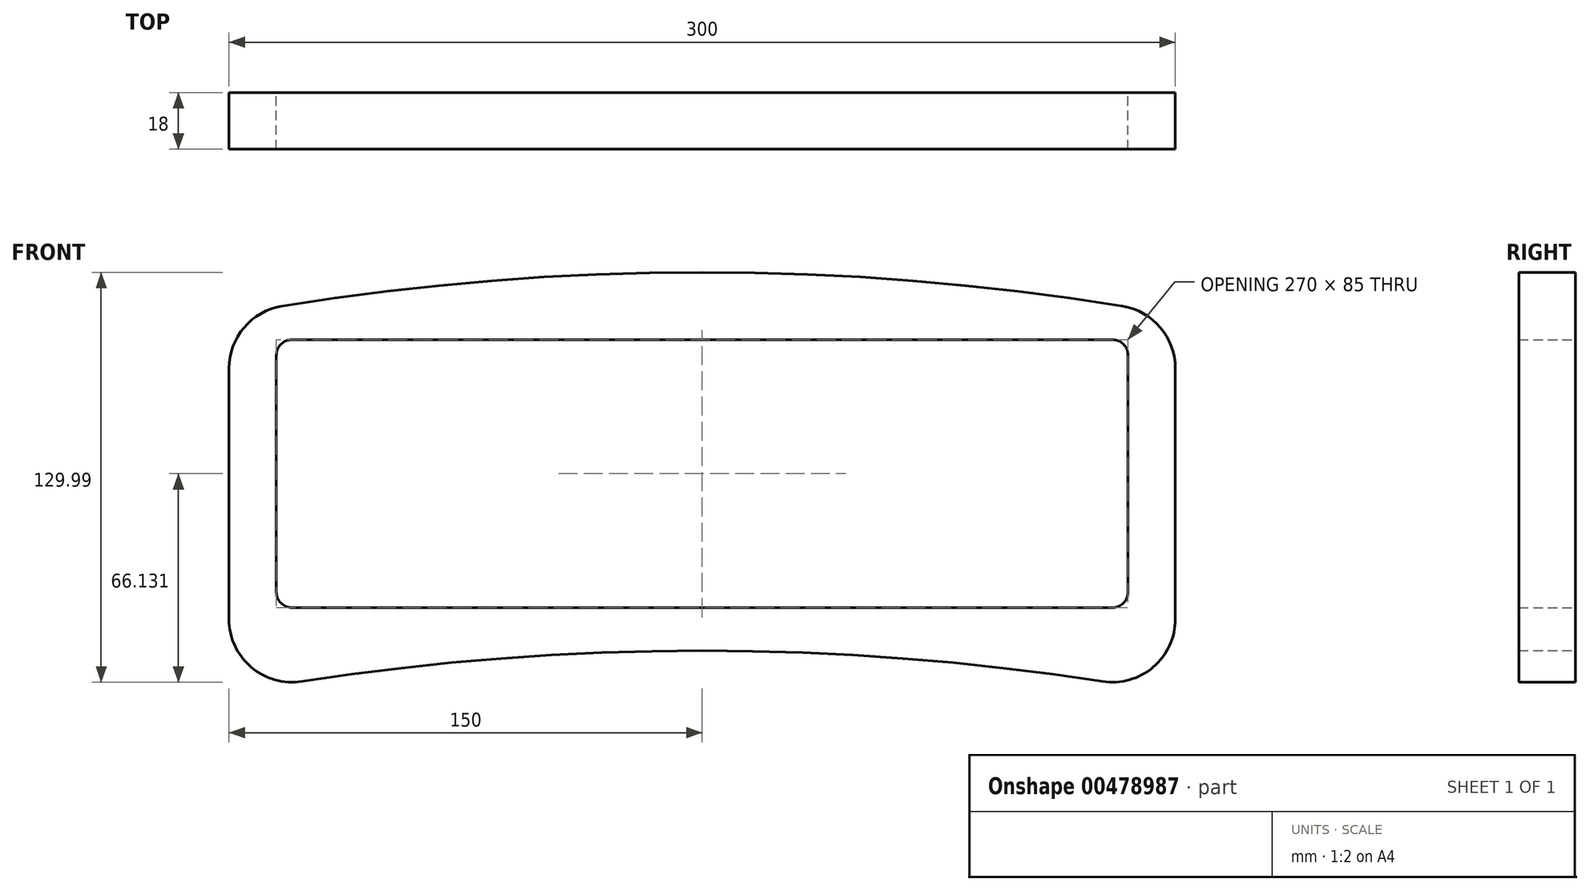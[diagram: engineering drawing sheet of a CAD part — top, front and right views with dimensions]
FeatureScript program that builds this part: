
annotation { "Feature Type Name" : "Feature", "Feature Type Description" : "" }
export const myFeature = defineFeature(function(context is Context, id is Id, definition is map)
    precondition{}
    {
        {
            var Q0;
            Q0=qCreatedBy(makeId("Front.planeOp"),FACE);
            var sketch = newSketch(context, id + "F0", { "sketchPlane" : qUnion([Q0])});
            skLineSegment(sketch, "E0", {"start": v(-80, 2.1) * mm, "end": v(80, 2.1) * mm, "construction": true});
            skLineSegment(sketch, "E1.bottom", {"start": v(-119, -36.9) * mm, "end": v(-41, -36.9) * mm, "construction": true});
            skLineSegment(sketch, "E1.top", {"start": v(-119, 41.1) * mm, "end": v(-41, 41.1) * mm, "construction": true});
            skLineSegment(sketch, "E1.left", {"start": v(-119, -36.9) * mm, "end": v(-119, 41.1) * mm, "construction": true});
            skLineSegment(sketch, "E1.right", {"start": v(-41, -36.9) * mm, "end": v(-41, 41.1) * mm, "construction": true});
            skPoint(sketch, "E1.middle", {"position": v(-80, 2.1) * mm});
            skLineSegment(sketch, "E2.bottom", {"start": v(119, -36.9) * mm, "end": v(41, -36.9) * mm, "construction": true});
            skLineSegment(sketch, "E2.top", {"start": v(119, 41.1) * mm, "end": v(41, 41.1) * mm, "construction": true});
            skLineSegment(sketch, "E2.left", {"start": v(119, -36.9) * mm, "end": v(119, 41.1) * mm, "construction": true});
            skLineSegment(sketch, "E2.right", {"start": v(41, -36.9) * mm, "end": v(41, 41.1) * mm, "construction": true});
            skPoint(sketch, "E2.middle", {"position": v(80, 2.1) * mm});
            skCircle(sketch, "E3", {"center": v(-80, 2.1) * mm, "radius": 37 * mm, "construction": true});
            skCircle(sketch, "E4", {"center": v(80, 2.1) * mm, "radius": 37 * mm, "construction": true});
            skLineSegment(sketch, "E5", {"start": v(-150, 35.47) * mm, "end": v(-150, -44.04) * mm});
            skLineSegment(sketch, "E6", {"start": v(0, 65.95) * mm, "end": v(0, -54.05) * mm, "construction": true});
            skLineSegment(sketch, "E7", {"start": v(150, 35.47) * mm, "end": v(150, -44.04) * mm});
            skPoint(sketch, "E8", {"position": v(-150, -7.7) * mm});
            skPoint(sketch, "E9", {"position": v(150, -7.7) * mm});
            skPoint(sketch, "E10", {"position": v(0, 5.95) * mm});
            skArc(sketch, "E11", {"start": v(133.2, 55.2) * mm, "mid": v(0, 65.95) * mm, "end": v(-133.2, 55.2) * mm});
            skArc(sketch, "E12", {"start": v(150, -7.7) * mm, "mid": v(0, 5.95) * mm, "end": v(-150, -7.7) * mm, "construction": true});
            skArc(sketch, "E13", {"start": v(126.95, -63.8) * mm, "mid": v(0, -54.05) * mm, "end": v(-126.95, -63.8) * mm});
            skPoint(sketch, "E14.visualSharp", {"position": v(-150, 52.3) * mm});
            skArc(sketch, "E14.filletArc", {"start": v(-133.2, 55.2) * mm, "mid": v(-145.23, 48.43) * mm, "end": v(-150, 35.47) * mm});
            skPoint(sketch, "E15.visualSharp", {"position": v(150, 52.3) * mm});
            skArc(sketch, "E15.filletArc", {"start": v(150, 35.47) * mm, "mid": v(145.23, 48.43) * mm, "end": v(133.2, 55.2) * mm});
            skPoint(sketch, "E16.visualSharp", {"position": v(150, -67.7) * mm});
            skArc(sketch, "E16.filletArc", {"start": v(126.95, -63.8) * mm, "mid": v(143.02, -59.22) * mm, "end": v(150, -44.04) * mm});
            skPoint(sketch, "E17.visualSharp", {"position": v(-150, -67.7) * mm});
            skArc(sketch, "E17.filletArc", {"start": v(-150, -44.04) * mm, "mid": v(-143.02, -59.22) * mm, "end": v(-126.95, -63.8) * mm});
            skLineSegment(sketch, "E18", {"start": v(-119, 41.1) * mm, "end": v(-41, -36.9) * mm, "construction": true});
            skLineSegment(sketch, "E19", {"start": v(-41, 41.1) * mm, "end": v(-119, -36.9) * mm, "construction": true});
            skLineSegment(sketch, "E20", {"start": v(41, 41.1) * mm, "end": v(119, -36.9) * mm, "construction": true});
            skLineSegment(sketch, "E21", {"start": v(119, 41.1) * mm, "end": v(41, -36.9) * mm, "construction": true});
            skCircle(sketch, "E22", {"center": v(-80, 2.1) * mm, "radius": 42.5 * mm, "construction": true});
            skCircle(sketch, "E23", {"center": v(80, 2.1) * mm, "radius": 42.5 * mm, "construction": true});
            skCircle(sketch, "E24", {"center": v(-49.95, 32.14) * mm, "radius": 2 * mm, "construction": true});
            skCircle(sketch, "E25", {"center": v(-110.05, 32.14) * mm, "radius": 2 * mm, "construction": true});
            skCircle(sketch, "E26", {"center": v(-110.05, -27.96) * mm, "radius": 2 * mm, "construction": true});
            skCircle(sketch, "E27", {"center": v(-49.95, -27.96) * mm, "radius": 2 * mm, "construction": true});
            skCircle(sketch, "E28", {"center": v(49.95, 32.14) * mm, "radius": 2 * mm, "construction": true});
            skCircle(sketch, "E29", {"center": v(49.95, -27.96) * mm, "radius": 2 * mm, "construction": true});
            skCircle(sketch, "E30", {"center": v(110.05, 32.14) * mm, "radius": 2 * mm, "construction": true});
            skCircle(sketch, "E31", {"center": v(110.05, -27.96) * mm, "radius": 2 * mm, "construction": true});
            skPoint(sketch, "E32", {"position": v(0, 2.1) * mm});
            skLineSegment(sketch, "E33.bottom", {"start": v(130, -40.4) * mm, "end": v(-130, -40.4) * mm});
            skLineSegment(sketch, "E33.top", {"start": v(130, 44.6) * mm, "end": v(-130, 44.6) * mm});
            skLineSegment(sketch, "E33.left", {"start": v(135, -35.4) * mm, "end": v(135, 39.6) * mm});
            skLineSegment(sketch, "E33.right", {"start": v(-135, -35.4) * mm, "end": v(-135, 39.6) * mm});
            skPoint(sketch, "E34.visualSharp", {"position": v(135, 44.6) * mm});
            skArc(sketch, "E34.filletArc", {"start": v(135, 39.6) * mm, "mid": v(133.54, 43.13) * mm, "end": v(130, 44.6) * mm});
            skPoint(sketch, "E35.visualSharp", {"position": v(135, -40.4) * mm});
            skArc(sketch, "E35.filletArc", {"start": v(130, -40.4) * mm, "mid": v(133.54, -38.94) * mm, "end": v(135, -35.4) * mm});
            skPoint(sketch, "E36.visualSharp", {"position": v(-135, -40.4) * mm});
            skArc(sketch, "E36.filletArc", {"start": v(-135, -35.4) * mm, "mid": v(-133.54, -38.94) * mm, "end": v(-130, -40.4) * mm});
            skPoint(sketch, "E37.visualSharp", {"position": v(-135, 44.6) * mm});
            skArc(sketch, "E37.filletArc", {"start": v(-130, 44.6) * mm, "mid": v(-133.54, 43.13) * mm, "end": v(-135, 39.6) * mm});
            skSolve(sketch);
        }
        {
            var Q0;
            Q0 = qSketchRegion(id + "F0", true);
            extrude(context, id + "F1", {"entities" : qUnion([Q0]), "depth" : 18 * mm});
        }
    });
